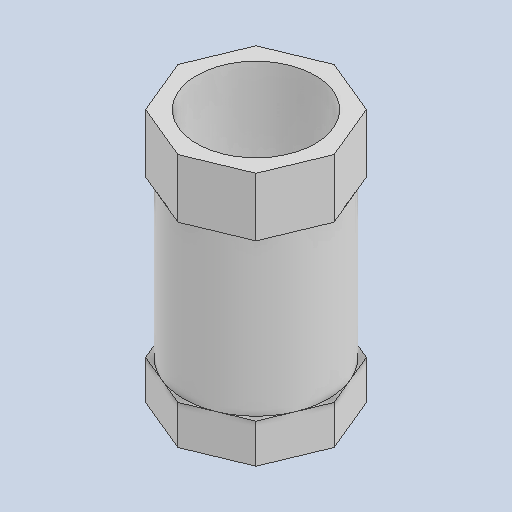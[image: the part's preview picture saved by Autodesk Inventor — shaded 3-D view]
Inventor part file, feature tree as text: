
AUTODESK INVENTOR PART (.ipt)
format: ipt  version: 2024 (Build 280153000, 153)  size: 148,480 bytes
history: native  units: mm
features: other x4, sketch x4
ambient origin geometry x8: Origin, YZ Plane, XZ Plane, XY Plane, X Axis, Y Axis, Z Axis, Center Point
bodies: Body1 (feature_tree)
feature tree (8):
  other  "TUBO_METALICO_B_MIR.ipt"
  other  "Sólido1::TUBO_METALICO_B_MIR.ipt"
  other  "OperaciónIdentificador1"
  sketch  "Boceto1"  dims[d0=10.0mm]
  sketch  "Boceto2"
  sketch  "Boceto3"
  sketch  "Boceto4"
  other  "Sólido1"
